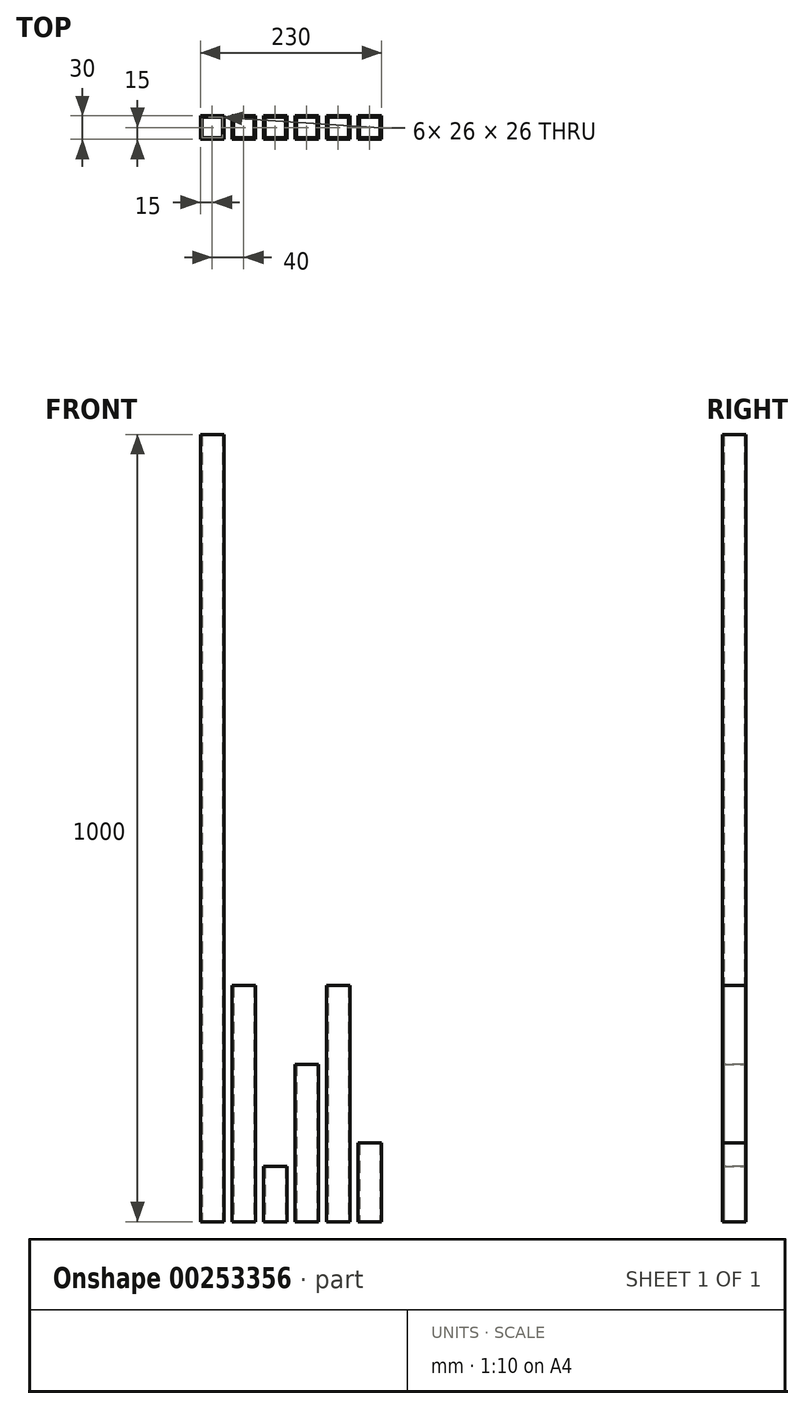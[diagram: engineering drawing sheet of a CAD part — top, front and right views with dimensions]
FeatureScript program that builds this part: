
annotation { "Feature Type Name" : "Feature", "Feature Type Description" : "" }
export const myFeature = defineFeature(function(context is Context, id is Id, definition is map)
    precondition{}
    {
        {
            assignVariable(context, id + "F0", {"name" : "Aussendurchmesser", "anyValue" : 30 * mm});
        }
        {
            assignVariable(context, id + "F1", {"name" : "Laenge1", "anyValue" : 1000 * mm});
        }
        {
            assignVariable(context, id + "F2", {"name" : "Laenge2", "anyValue" : 300 * mm});
        }
        {
            assignVariable(context, id + "F3", {"name" : "Laenge3", "anyValue" : 70 * mm});
        }
        {
            assignVariable(context, id + "F4", {"name" : "Laenge4", "anyValue" : 200 * mm});
        }
        {
            assignVariable(context, id + "F5", {"name" : "Laenge5", "anyValue" : 100 * mm});
        }
        {
            var Q0;
            Q0=qCreatedBy(makeId("Top.planeOp"),FACE);
            var sketch = newSketch(context, id + "F6", { "sketchPlane" : qUnion([Q0])});
            skLineSegment(sketch, "E0.bottom", {"start": v(0, 0) * mm, "end": v(30, 0) * mm});
            skLineSegment(sketch, "E0.top", {"start": v(0, 30) * mm, "end": v(30, 30) * mm});
            skLineSegment(sketch, "E0.left", {"start": v(0, 0) * mm, "end": v(0, 30) * mm});
            skLineSegment(sketch, "E0.right", {"start": v(30, 0) * mm, "end": v(30, 30) * mm});
            skLineSegment(sketch, "E1.bottom", {"start": v(80, 0) * mm, "end": v(110, 0) * mm});
            skLineSegment(sketch, "E1.top", {"start": v(80, 30) * mm, "end": v(110, 30) * mm});
            skLineSegment(sketch, "E1.left", {"start": v(80, 0) * mm, "end": v(80, 30) * mm});
            skLineSegment(sketch, "E1.right", {"start": v(110, 0) * mm, "end": v(110, 30) * mm});
            skLineSegment(sketch, "E2.bottom", {"start": v(40, 0) * mm, "end": v(70, 0) * mm});
            skLineSegment(sketch, "E2.top", {"start": v(40, 30) * mm, "end": v(70, 30) * mm});
            skLineSegment(sketch, "E2.left", {"start": v(40, 0) * mm, "end": v(40, 30) * mm});
            skLineSegment(sketch, "E2.right", {"start": v(70, 0) * mm, "end": v(70, 30) * mm});
            skLineSegment(sketch, "E3.bottom", {"start": v(120, 0) * mm, "end": v(150, 0) * mm});
            skLineSegment(sketch, "E3.top", {"start": v(120, 30) * mm, "end": v(150, 30) * mm});
            skLineSegment(sketch, "E3.left", {"start": v(120, 0) * mm, "end": v(120, 30) * mm});
            skLineSegment(sketch, "E3.right", {"start": v(150, 0) * mm, "end": v(150, 30) * mm});
            skLineSegment(sketch, "E4.bottom", {"start": v(160, 0) * mm, "end": v(190, 0) * mm});
            skLineSegment(sketch, "E4.top", {"start": v(160, 30) * mm, "end": v(190, 30) * mm});
            skLineSegment(sketch, "E4.left", {"start": v(160, 0) * mm, "end": v(160, 30) * mm});
            skLineSegment(sketch, "E4.right", {"start": v(190, 0) * mm, "end": v(190, 30) * mm});
            skLineSegment(sketch, "E5.bottom", {"start": v(188, 28) * mm, "end": v(162, 28) * mm});
            skLineSegment(sketch, "E5.top", {"start": v(188, 2) * mm, "end": v(162, 2) * mm});
            skLineSegment(sketch, "E5.left", {"start": v(188, 28) * mm, "end": v(188, 2) * mm});
            skLineSegment(sketch, "E5.right", {"start": v(162, 28) * mm, "end": v(162, 2) * mm});
            skPoint(sketch, "E5.middle", {"position": v(175, 15) * mm});
            skPoint(sketch, "E5.middle.positionSnap0", {"position": v(160, 15) * mm});
            skPoint(sketch, "E5.middle.positionSnap1", {"position": v(175, 0) * mm});
            skPoint(sketch, "E5.centerSnap0", {"position": v(160, 15) * mm});
            skPoint(sketch, "E5.centerSnap1", {"position": v(175, 0) * mm});
            skLineSegment(sketch, "E6.bottom", {"start": v(28, 28) * mm, "end": v(2, 28) * mm});
            skLineSegment(sketch, "E6.top", {"start": v(28, 2) * mm, "end": v(2, 2) * mm});
            skLineSegment(sketch, "E6.left", {"start": v(28, 28) * mm, "end": v(28, 2) * mm});
            skLineSegment(sketch, "E6.right", {"start": v(2, 28) * mm, "end": v(2, 2) * mm});
            skPoint(sketch, "E6.middle", {"position": v(15, 15) * mm});
            skPoint(sketch, "E6.middle.positionSnap0", {"position": v(0, 15) * mm});
            skPoint(sketch, "E6.middle.positionSnap1", {"position": v(15, 0) * mm});
            skPoint(sketch, "E6.centerSnap0", {"position": v(0, 15) * mm});
            skPoint(sketch, "E6.centerSnap1", {"position": v(15, 0) * mm});
            skLineSegment(sketch, "E7.bottom", {"start": v(68, 28) * mm, "end": v(42, 28) * mm});
            skLineSegment(sketch, "E7.top", {"start": v(68, 2) * mm, "end": v(42, 2) * mm});
            skLineSegment(sketch, "E7.left", {"start": v(68, 28) * mm, "end": v(68, 2) * mm});
            skLineSegment(sketch, "E7.right", {"start": v(42, 28) * mm, "end": v(42, 2) * mm});
            skPoint(sketch, "E7.middle", {"position": v(55, 15) * mm});
            skPoint(sketch, "E7.middle.positionSnap0", {"position": v(55, 0) * mm});
            skPoint(sketch, "E7.middle.positionSnap1", {"position": v(40, 15) * mm});
            skPoint(sketch, "E7.centerSnap0", {"position": v(55, 0) * mm});
            skPoint(sketch, "E7.centerSnap1", {"position": v(40, 15) * mm});
            skLineSegment(sketch, "E8.bottom", {"start": v(108, 28) * mm, "end": v(82, 28) * mm});
            skLineSegment(sketch, "E8.top", {"start": v(108, 2) * mm, "end": v(82, 2) * mm});
            skLineSegment(sketch, "E8.left", {"start": v(108, 28) * mm, "end": v(108, 2) * mm});
            skLineSegment(sketch, "E8.right", {"start": v(82, 28) * mm, "end": v(82, 2) * mm});
            skPoint(sketch, "E8.middle", {"position": v(95, 15) * mm});
            skPoint(sketch, "E8.middle.positionSnap0", {"position": v(80, 15) * mm});
            skPoint(sketch, "E8.middle.positionSnap1", {"position": v(95, 0) * mm});
            skPoint(sketch, "E8.centerSnap0", {"position": v(80, 15) * mm});
            skPoint(sketch, "E8.centerSnap1", {"position": v(95, 0) * mm});
            skLineSegment(sketch, "E9.bottom", {"start": v(148, 28) * mm, "end": v(122, 28) * mm});
            skLineSegment(sketch, "E9.top", {"start": v(148, 2) * mm, "end": v(122, 2) * mm});
            skLineSegment(sketch, "E9.left", {"start": v(148, 28) * mm, "end": v(148, 2) * mm});
            skLineSegment(sketch, "E9.right", {"start": v(122, 28) * mm, "end": v(122, 2) * mm});
            skPoint(sketch, "E9.middle", {"position": v(135, 15) * mm});
            skPoint(sketch, "E9.middle.positionSnap0", {"position": v(120, 15) * mm});
            skPoint(sketch, "E9.middle.positionSnap1", {"position": v(135, 0) * mm});
            skPoint(sketch, "E9.centerSnap0", {"position": v(120, 15) * mm});
            skPoint(sketch, "E9.centerSnap1", {"position": v(135, 0) * mm});
            skLineSegment(sketch, "E10.bottom", {"start": v(200, 0) * mm, "end": v(230, 0) * mm});
            skLineSegment(sketch, "E10.top", {"start": v(200, 30) * mm, "end": v(230, 30) * mm});
            skLineSegment(sketch, "E10.left", {"start": v(200, 0) * mm, "end": v(200, 30) * mm});
            skLineSegment(sketch, "E10.right", {"start": v(230, 0) * mm, "end": v(230, 30) * mm});
            skLineSegment(sketch, "E11.bottom", {"start": v(202, 28) * mm, "end": v(228, 28) * mm});
            skLineSegment(sketch, "E11.top", {"start": v(202, 2) * mm, "end": v(228, 2) * mm});
            skLineSegment(sketch, "E11.left", {"start": v(202, 28) * mm, "end": v(202, 2) * mm});
            skLineSegment(sketch, "E11.right", {"start": v(228, 28) * mm, "end": v(228, 2) * mm});
            skPoint(sketch, "E11.middle", {"position": v(215, 15) * mm});
            skPoint(sketch, "E11.middle.positionSnap0", {"position": v(215, 0) * mm});
            skPoint(sketch, "E11.middle.positionSnap1", {"position": v(200, 15) * mm});
            skPoint(sketch, "E11.centerSnap0", {"position": v(215, 0) * mm});
            skPoint(sketch, "E11.centerSnap1", {"position": v(200, 15) * mm});
            skPoint(sketch, "E12.oppositeSnap0", {"position": v(215, 30) * mm});
            skSolve(sketch);
        }
        {
            var Q0;
            Q0=makeQuery(id+"F6.imprint","IMPRINT",FACE,{"disambiguationData":[TD([[makeQuery(id+"F6.imprint","IMPRINT",EDGE,{"derivedFrom":sQuery(id+"F6.wireOp",EDGE,"E0.bottom")}),1.0]])]});
            extrude(context, id + "F7", {"entities" : qUnion([Q0]), "depth" : getVariable(context, 'Laenge1')});
        }
        {
            var Q0;
            Q0=makeQuery(id+"F6.imprint","IMPRINT",FACE,{"disambiguationData":[TD([[makeQuery(id+"F6.imprint","IMPRINT",EDGE,{"derivedFrom":sQuery(id+"F6.wireOp",EDGE,"E2.bottom")}),1.0]])]});
            extrude(context, id + "F8", {"entities" : qUnion([Q0]), "depth" : getVariable(context, 'Laenge2')});
        }
        {
            var Q0;
            Q0=makeQuery(id+"F6.imprint","IMPRINT",FACE,{"disambiguationData":[TD([[makeQuery(id+"F6.imprint","IMPRINT",EDGE,{"derivedFrom":sQuery(id+"F6.wireOp",EDGE,"E1.bottom")}),1.0]])]});
            extrude(context, id + "F9", {"entities" : qUnion([Q0]), "depth" : getVariable(context, 'Laenge3')});
        }
        {
            var Q0;
            Q0=makeQuery(id+"F6.imprint","IMPRINT",FACE,{"disambiguationData":[TD([[makeQuery(id+"F6.imprint","IMPRINT",EDGE,{"derivedFrom":sQuery(id+"F6.wireOp",EDGE,"E3.bottom")}),1.0]])]});
            extrude(context, id + "F10", {"entities" : qUnion([Q0]), "depth" : getVariable(context, 'Laenge4')});
        }
        {
            var Q0;
            Q0=makeQuery(id+"F6.imprint","IMPRINT",FACE,{"disambiguationData":[TD([[makeQuery(id+"F6.imprint","IMPRINT",EDGE,{"derivedFrom":sQuery(id+"F6.wireOp",EDGE,"E4.bottom")}),1.0]])]});
            extrude(context, id + "F11", {"entities" : qUnion([Q0]), "depth" : getVariable(context, 'Laenge4') + 70 * mm + getVariable(context, 'Aussendurchmesser')});
        }
        {
            var Q0;
            Q0=makeQuery(id+"F6.imprint","IMPRINT",FACE,{"disambiguationData":[TD([[makeQuery(id+"F6.imprint","IMPRINT",EDGE,{"derivedFrom":sQuery(id+"F6.wireOp",EDGE,"E10.bottom")}),1.0]])]});
            extrude(context, id + "F12", {"entities" : qUnion([Q0]), "depth" : getVariable(context, 'Laenge5')});
        }
    });
